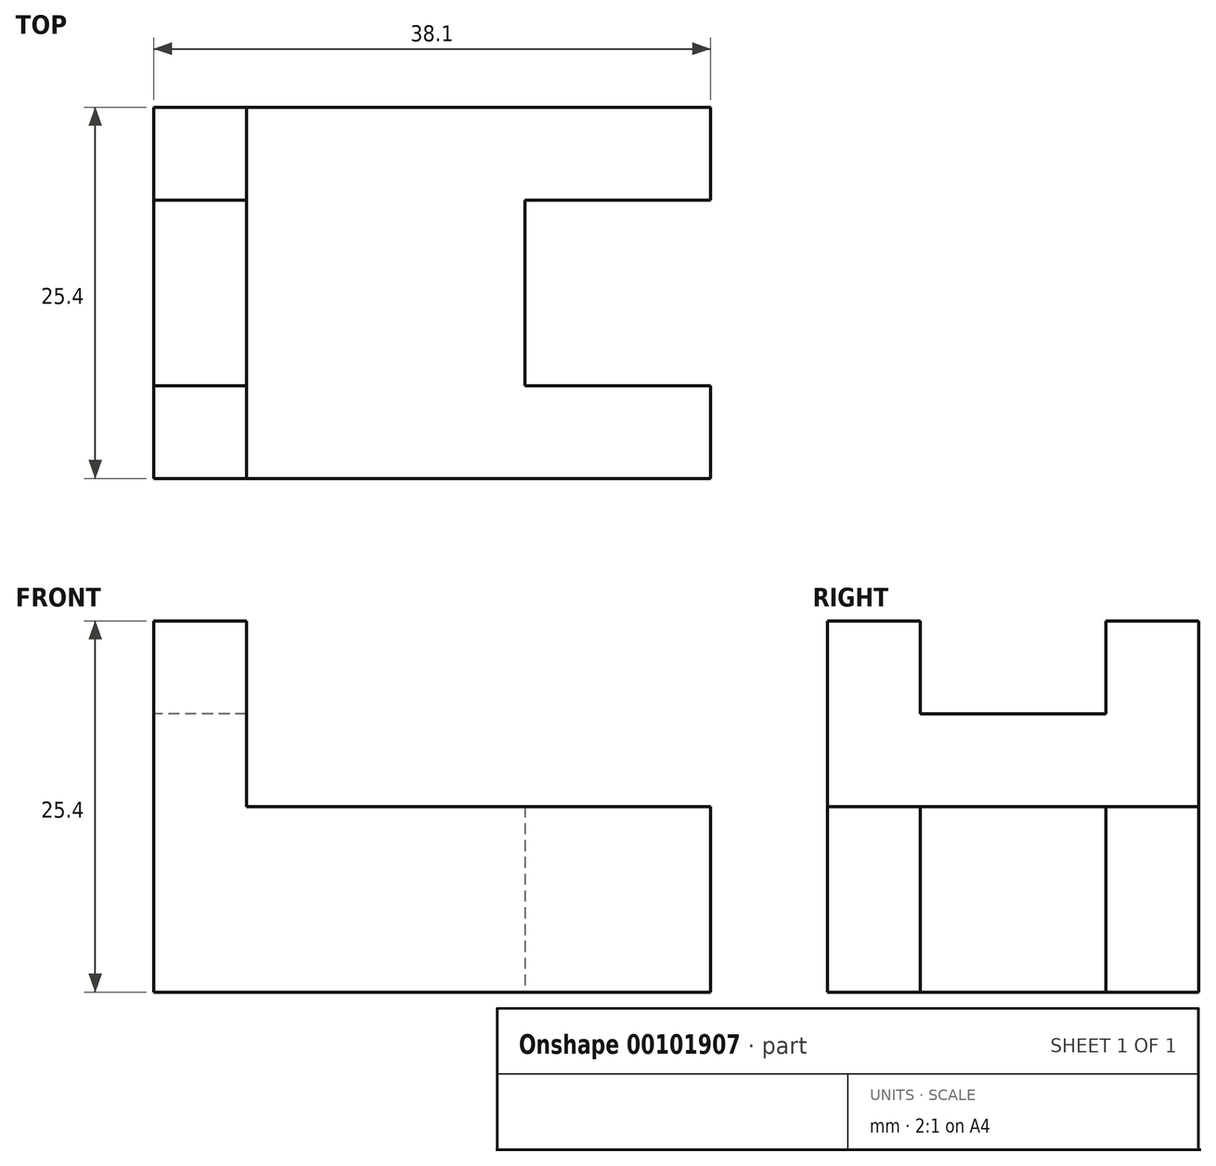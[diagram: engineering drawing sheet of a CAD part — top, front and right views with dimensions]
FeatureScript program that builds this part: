
annotation { "Feature Type Name" : "Feature", "Feature Type Description" : "" }
export const myFeature = defineFeature(function(context is Context, id is Id, definition is map)
    precondition{}
    {
        {
            var Q0;
            Q0=qCreatedBy(makeId("Top.planeOp"),FACE);
            var sketch = newSketch(context, id + "F0", { "sketchPlane" : qUnion([Q0])});
            skLineSegment(sketch, "E0", {"start": v(0, 0) * mm, "end": v(0, -25.4) * mm});
            skLineSegment(sketch, "E1", {"start": v(0, -25.4) * mm, "end": v(38.1, -25.4) * mm});
            skLineSegment(sketch, "E2", {"start": v(38.1, -25.4) * mm, "end": v(38.1, -19.05) * mm});
            skLineSegment(sketch, "E3", {"start": v(38.1, -19.05) * mm, "end": v(25.4, -19.05) * mm});
            skLineSegment(sketch, "E4", {"start": v(25.4, -19.05) * mm, "end": v(25.4, -6.35) * mm});
            skLineSegment(sketch, "E5", {"start": v(25.4, -6.35) * mm, "end": v(38.1, -6.35) * mm});
            skLineSegment(sketch, "E6", {"start": v(38.1, -6.35) * mm, "end": v(38.1, 0) * mm});
            skLineSegment(sketch, "E7", {"start": v(38.1, 0) * mm, "end": v(0, 0) * mm});
            skSolve(sketch);
        }
        {
            var Q0;
            Q0 = qSketchRegion(id + "F0", true);
            extrude(context, id + "F1", {"entities" : qUnion([Q0]), "depth" : 12.7 * mm});
        }
        {
            var Q0;
            Q0=makeQuery(id+"F1.opExtrude","SWEPT_FACE",FACE,{"disambiguationData":[OSD([sQuery(id+"F0.wireOp",EDGE,"E0")])]});
            var sketch = newSketch(context, id + "F2", { "sketchPlane" : qUnion([Q0])});
            skLineSegment(sketch, "E8", {"start": v(0, 10.31) * mm, "end": v(0, 25.4) * mm});
            skLineSegment(sketch, "E9", {"start": v(0, 25.4) * mm, "end": v(6.35, 25.4) * mm});
            skLineSegment(sketch, "E10", {"start": v(6.35, 25.4) * mm, "end": v(6.35, 19.05) * mm});
            skLineSegment(sketch, "E11", {"start": v(6.35, 19.05) * mm, "end": v(19.05, 19.05) * mm});
            skLineSegment(sketch, "E12", {"start": v(19.05, 19.05) * mm, "end": v(19.05, 25.4) * mm});
            skLineSegment(sketch, "E13", {"start": v(19.05, 25.4) * mm, "end": v(25.4, 25.4) * mm});
            skLineSegment(sketch, "E14", {"start": v(25.4, 25.4) * mm, "end": v(25.4, 10.31) * mm});
            skLineSegment(sketch, "E15", {"start": v(25.4, 10.31) * mm, "end": v(0, 10.31) * mm});
            skSolve(sketch);
        }
        {
            var Q0;
            Q0 = qSketchRegion(id + "F2", true);
            extrude(context, id + "F3", {"entities" : qUnion([Q0]), "operationType" : NewBodyOperationType.ADD, "oppositeDirection" : true, "depth" : 6.35 * mm});
        }
    });
